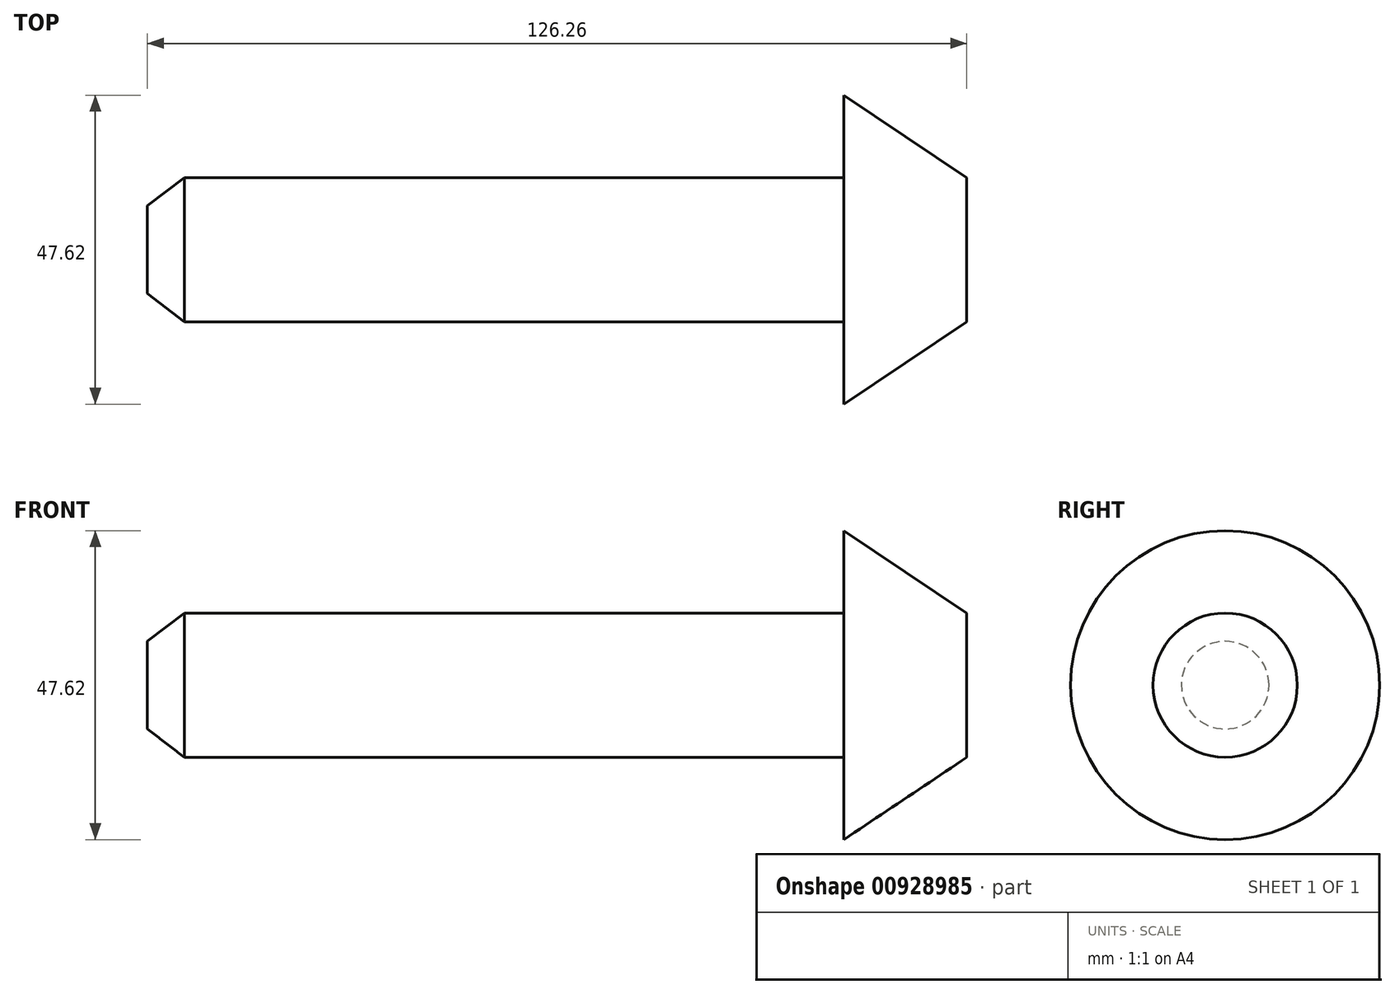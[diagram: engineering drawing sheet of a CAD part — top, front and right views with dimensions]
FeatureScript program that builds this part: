
annotation { "Feature Type Name" : "Feature", "Feature Type Description" : "" }
export const myFeature = defineFeature(function(context is Context, id is Id, definition is map)
    precondition{}
    {
        {
            var Q0;
            Q0=qCreatedBy(makeId("Front.planeOp"),FACE);
            var sketch = newSketch(context, id + "F0", { "sketchPlane" : qUnion([Q0])});
            skLineSegment(sketch, "E0", {"start": v(0, 11.11) * mm, "end": v(0, 23.81) * mm});
            skLineSegment(sketch, "E1", {"start": v(0, 23.81) * mm, "end": v(18.95, 11.11) * mm});
            skLineSegment(sketch, "E2", {"start": v(18.95, 11.11) * mm, "end": v(18.95, 0) * mm});
            skLineSegment(sketch, "E3", {"start": v(18.95, 0) * mm, "end": v(-107.3, 0) * mm});
            skLineSegment(sketch, "E4", {"start": v(-107.3, 0) * mm, "end": v(-107.3, 6.75) * mm});
            skLineSegment(sketch, "E5", {"start": v(-107.3, 6.75) * mm, "end": v(-101.6, 11.11) * mm});
            skLineSegment(sketch, "E6", {"start": v(-101.6, 11.11) * mm, "end": v(0, 11.11) * mm});
            skSolve(sketch);
        }
        {
            var Q0;
            Q0 = qSketchRegion(id + "F0", true);
            var Q1;
            Q1=sQuery(id+"F0.wireOp",EDGE,"E3");
            revolve(context, id + "F1", {"surfaceOperationType" : NewSurfaceOperationType.NEW, "entities" : qUnion([Q0]), "axis" : qUnion([Q1]), "revolveType" : RevolveType.FULL});
        }
    });
